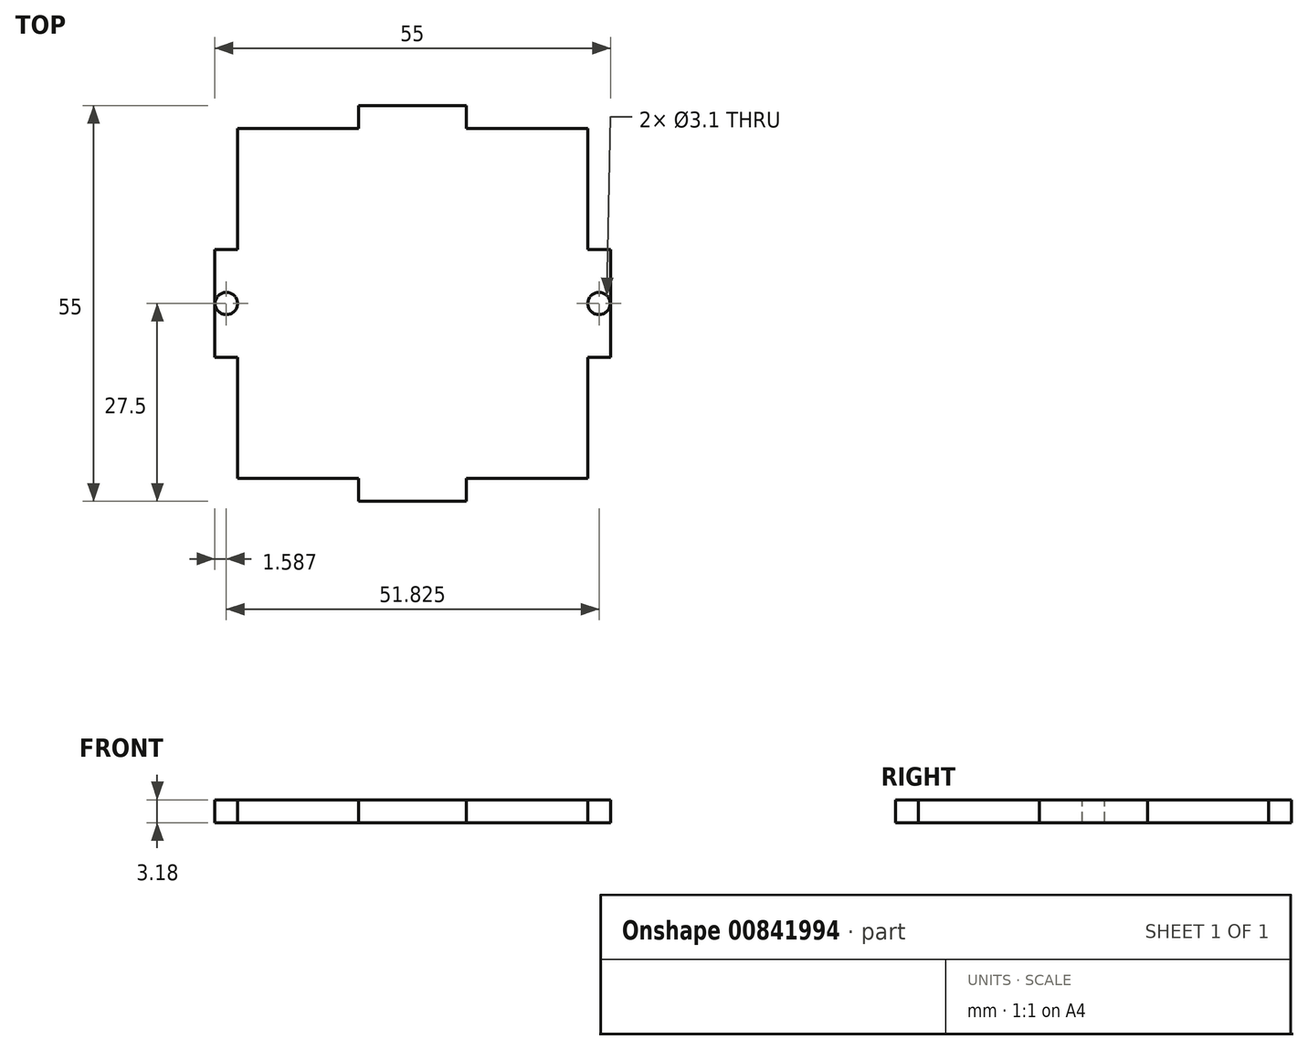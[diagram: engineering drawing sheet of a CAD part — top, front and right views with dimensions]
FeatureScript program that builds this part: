
annotation { "Feature Type Name" : "Feature", "Feature Type Description" : "" }
export const myFeature = defineFeature(function(context is Context, id is Id, definition is map)
    precondition{}
    {
        {
            assignVariable(context, id + "F0", {"name" : "mat_t", "anyValue" : 3.17});
        }
        {
            var Q0;
            Q0=qCreatedBy(makeId("Top.planeOp"),FACE);
            var sketch = newSketch(context, id + "F1", { "sketchPlane" : qUnion([Q0])});
            skLineSegment(sketch, "E0.bottom", {"start": v(24.33, -24.32) * mm, "end": v(-24.32, -24.33) * mm});
            skLineSegment(sketch, "E0.top", {"start": v(24.32, 24.33) * mm, "end": v(-24.33, 24.32) * mm});
            skLineSegment(sketch, "E0.left", {"start": v(24.33, -24.32) * mm, "end": v(24.32, 24.33) * mm});
            skLineSegment(sketch, "E0.right", {"start": v(-24.32, -24.33) * mm, "end": v(-24.33, 24.32) * mm});
            skPoint(sketch, "E0.middle", {"position": v(0, 0) * mm});
            skSolve(sketch);
        }
        {
            var Q0;
            Q0=qSketchRegion(id+"F1",true);
            extrude(context, id + "F2", {"entities" : qUnion([Q0]), "depth" : (getVariable(context, 'mat_t')) * mm, "offsetDistance" : 25 * mm});
        }
        {
            var Q0;
            Q0=makeQuery(id+"F2.opExtrude","CAP_FACE",FACE,{"disambiguationData":[OSD([sQuery(id+"F1.wireOp",EDGE,"E0.bottom"),sQuery(id+"F1.wireOp",EDGE,"E0.top"),sQuery(id+"F1.wireOp",EDGE,"E0.left"),sQuery(id+"F1.wireOp",EDGE,"E0.right")])],"isStart":false});
            var sketch = newSketch(context, id + "F3", { "sketchPlane" : qUnion([Q0])});
            skLineSegment(sketch, "E1", {"start": v(0, 24.32) * mm, "end": v(0, -24.32) * mm, "construction": true});
            skLineSegment(sketch, "E2", {"start": v(-24.32, 0) * mm, "end": v(24.32, 0) * mm, "construction": true});
            skLineSegment(sketch, "E3.bottom", {"start": v(-24.32, 7.5) * mm, "end": v(-27.5, 7.5) * mm});
            skLineSegment(sketch, "E3.top", {"start": v(-24.32, -7.5) * mm, "end": v(-27.5, -7.5) * mm});
            skLineSegment(sketch, "E3.left", {"start": v(-24.32, 7.5) * mm, "end": v(-24.32, -7.5) * mm});
            skLineSegment(sketch, "E3.right", {"start": v(-27.5, 7.5) * mm, "end": v(-27.5, -7.5) * mm});
            skLineSegment(sketch, "E4.bottom", {"start": v(-7.5, 24.32) * mm, "end": v(7.5, 24.32) * mm});
            skLineSegment(sketch, "E4.top", {"start": v(-7.5, 27.5) * mm, "end": v(7.5, 27.5) * mm});
            skLineSegment(sketch, "E4.left", {"start": v(-7.5, 24.32) * mm, "end": v(-7.5, 27.5) * mm});
            skLineSegment(sketch, "E4.right", {"start": v(7.5, 24.33) * mm, "end": v(7.5, 27.5) * mm});
            skLineSegment(sketch, "E5.MirrorCS", {"start": v(7.5, -24.32) * mm, "end": v(7.5, -27.5) * mm});
            skLineSegment(sketch, "E6.MirrorCS", {"start": v(-7.5, -24.32) * mm, "end": v(-7.5, -27.5) * mm});
            skLineSegment(sketch, "E7.MirrorCS", {"start": v(-7.5, -24.33) * mm, "end": v(7.5, -24.32) * mm});
            skLineSegment(sketch, "E8.MirrorCS", {"start": v(-7.5, -27.5) * mm, "end": v(7.5, -27.5) * mm});
            skLineSegment(sketch, "E9.MirrorCS", {"start": v(27.5, 7.5) * mm, "end": v(27.5, -7.5) * mm});
            skLineSegment(sketch, "E10.MirrorCS", {"start": v(24.32, -7.5) * mm, "end": v(27.5, -7.5) * mm});
            skLineSegment(sketch, "E11.MirrorCS", {"start": v(24.32, 7.5) * mm, "end": v(24.32, -7.5) * mm});
            skLineSegment(sketch, "E12.MirrorCS", {"start": v(24.32, 7.5) * mm, "end": v(27.5, 7.5) * mm});
            skSolve(sketch);
        }
        {
            var Q0;
            Q0=qSketchRegion(id+"F3",true);
            var Q1;
            Q1=makeQuery(id+"F2.opExtrude","CAP_FACE",FACE,{"disambiguationData":[OSD([sQuery(id+"F1.wireOp",EDGE,"E0.bottom"),sQuery(id+"F1.wireOp",EDGE,"E0.top"),sQuery(id+"F1.wireOp",EDGE,"E0.left"),sQuery(id+"F1.wireOp",EDGE,"E0.right")])],"isStart":true});
            extrude(context, id + "F4", {"entities" : qUnion([Q0]), "operationType" : NewBodyOperationType.ADD, "endBound" : BoundingType.UP_TO_SURFACE, "oppositeDirection" : true, "depth" : 25 * mm, "endBoundEntityFace" : qUnion([Q1]), "offsetDistance" : 25 * mm});
        }
        {
            var Q0;
            Q0=makeQuery(id+"F4.boolean.opBoolean","MERGE",FACE,{"derivedFrom":[makeQuery(id+"F2.opExtrude","CAP_FACE",FACE,{"disambiguationData":[OSD([sQuery(id+"F1.wireOp",EDGE,"E0.bottom"),sQuery(id+"F1.wireOp",EDGE,"E0.top"),sQuery(id+"F1.wireOp",EDGE,"E0.left"),sQuery(id+"F1.wireOp",EDGE,"E0.right")])],"isStart":false}),makeQuery(id+"F4.opExtrude","CAP_FACE",FACE,{"disambiguationData":[OSD([sQuery(id+"F3.wireOp",EDGE,"E3.bottom"),sQuery(id+"F3.wireOp",EDGE,"E3.top"),sQuery(id+"F3.wireOp",EDGE,"E3.left"),sQuery(id+"F3.wireOp",EDGE,"E3.right")])],"isStart":true}),makeQuery(id+"F4.opExtrude","CAP_FACE",FACE,{"disambiguationData":[OSD([sQuery(id+"F3.wireOp",EDGE,"E4.bottom"),sQuery(id+"F3.wireOp",EDGE,"E4.top"),sQuery(id+"F3.wireOp",EDGE,"E4.left"),sQuery(id+"F3.wireOp",EDGE,"E4.right")])],"isStart":true}),makeQuery(id+"F4.opExtrude","CAP_FACE",FACE,{"disambiguationData":[OSD([sQuery(id+"F3.wireOp",EDGE,"E5.MirrorCS"),sQuery(id+"F3.wireOp",EDGE,"E6.MirrorCS"),sQuery(id+"F3.wireOp",EDGE,"E7.MirrorCS"),sQuery(id+"F3.wireOp",EDGE,"E8.MirrorCS")])],"isStart":true}),makeQuery(id+"F4.opExtrude","CAP_FACE",FACE,{"disambiguationData":[OSD([sQuery(id+"F3.wireOp",EDGE,"E9.MirrorCS"),sQuery(id+"F3.wireOp",EDGE,"E10.MirrorCS"),sQuery(id+"F3.wireOp",EDGE,"E11.MirrorCS"),sQuery(id+"F3.wireOp",EDGE,"E12.MirrorCS")])],"isStart":true})]});
            var sketch = newSketch(context, id + "F5", { "sketchPlane" : qUnion([Q0])});
            skLineSegment(sketch, "E13", {"start": v(-27.5, 0) * mm, "end": v(27.5, 0) * mm, "construction": true});
            skLineSegment(sketch, "E14", {"start": v(0, 27.5) * mm, "end": v(0, -27.5) * mm, "construction": true});
            skLineSegment(sketch, "E15", {"start": v(-25.91, 7.5) * mm, "end": v(-25.91, -7.5) * mm, "construction": true});
            skCircle(sketch, "E16", {"center": v(-25.91, 0) * mm, "radius": 1.55 * mm});
            skCircle(sketch, "E17.MirrorC", {"center": v(25.91, 0) * mm, "radius": 1.55 * mm});
            skSolve(sketch);
        }
        {
            var Q0;
            Q0 = qSketchRegion(id + "F5", true);
            extrude(context, id + "F6", {"entities" : qUnion([Q0]), "operationType" : NewBodyOperationType.REMOVE, "endBound" : BoundingType.THROUGH_ALL, "oppositeDirection" : true, "depth" : 25 * mm, "offsetDistance" : 25 * mm});
        }
    });
